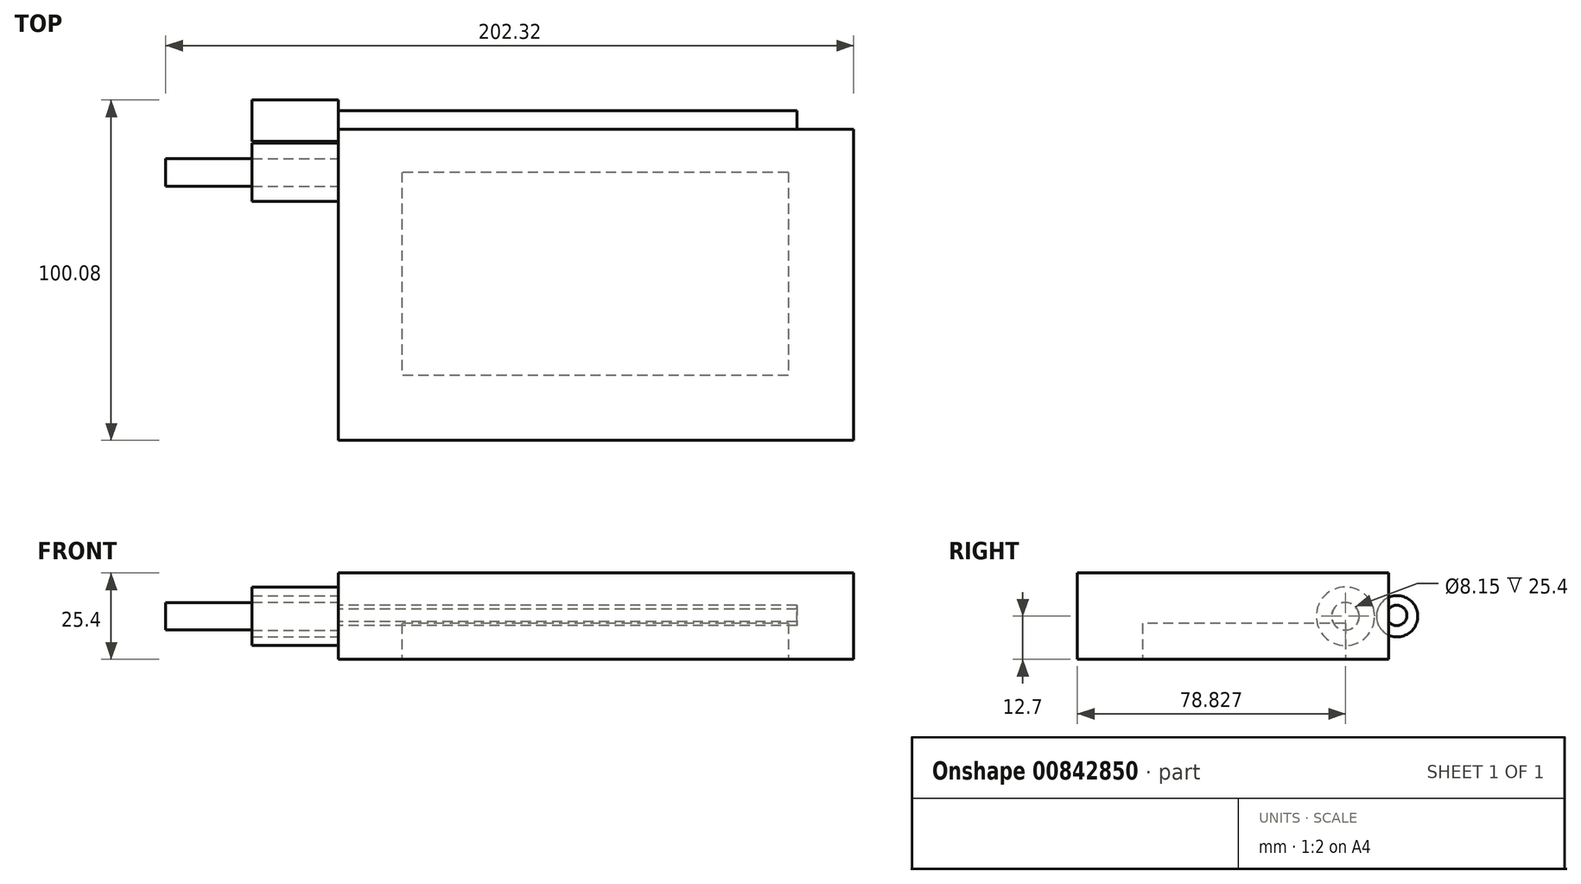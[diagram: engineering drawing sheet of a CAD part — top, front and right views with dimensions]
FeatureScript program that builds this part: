
annotation { "Feature Type Name" : "Feature", "Feature Type Description" : "" }
export const myFeature = defineFeature(function(context is Context, id is Id, definition is map)
    precondition{}
    {
        {
            var Q0;
            Q0=qCreatedBy(makeId("Top.planeOp"),FACE);
            var sketch = newSketch(context, id + "F0", { "sketchPlane" : qUnion([Q0])});
            skLineSegment(sketch, "E0.bottom", {"start": v(-75.46, -48.99) * mm, "end": v(76.06, -48.99) * mm});
            skLineSegment(sketch, "E0.top", {"start": v(-75.46, 42.56) * mm, "end": v(76.06, 42.56) * mm});
            skLineSegment(sketch, "E0.left", {"start": v(-75.46, -48.99) * mm, "end": v(-75.46, 42.56) * mm});
            skLineSegment(sketch, "E0.right", {"start": v(76.06, -48.99) * mm, "end": v(76.06, 42.56) * mm});
            skSolve(sketch);
        }
        {
            var Q0;
            Q0=makeQuery(id+"F0.imprint","IMPRINT",FACE,{"disambiguationData":[TD([[makeQuery(id+"F0.imprint","IMPRINT",EDGE,{"derivedFrom":sQuery(id+"F0.wireOp",EDGE,"E0.bottom")}),1.0]])]});
            extrude(context, id + "F1", {"entities" : qUnion([Q0]), "depth" : 25.4 * mm, "offsetDistance" : 25.4 * mm});
        }
        {
            var Q0;
            Q0=makeQuery(id+"F1.opExtrude","CAP_FACE",FACE,{"disambiguationData":[OSD([sQuery(id+"F0.wireOp",EDGE,"E0.bottom"),sQuery(id+"F0.wireOp",EDGE,"E0.top"),sQuery(id+"F0.wireOp",EDGE,"E0.left"),sQuery(id+"F0.wireOp",EDGE,"E0.right")])],"isStart":true});
            var sketch = newSketch(context, id + "F2", { "sketchPlane" : qUnion([Q0])});
            skLineSegment(sketch, "E1.bottom", {"start": v(56.8, -29.83) * mm, "end": v(-56.8, -29.83) * mm});
            skLineSegment(sketch, "E1.top", {"start": v(56.8, 29.83) * mm, "end": v(-56.8, 29.83) * mm});
            skLineSegment(sketch, "E1.left", {"start": v(56.8, -29.83) * mm, "end": v(56.8, 29.83) * mm});
            skLineSegment(sketch, "E1.right", {"start": v(-56.8, -29.83) * mm, "end": v(-56.8, 29.83) * mm});
            skPoint(sketch, "E1.middle", {"position": v(0, 0) * mm});
            skSolve(sketch);
        }
        {
            var Q0;
            Q0 = qSketchRegion(id + "F2", true);
            extrude(context, id + "F3", {"entities" : qUnion([Q0]), "operationType" : NewBodyOperationType.REMOVE, "oppositeDirection" : true, "depth" : 10.56 * mm, "offsetDistance" : 25.4 * mm});
        }
        {
            var Q0;
            Q0=makeQuery(id+"F1.opExtrude","SWEPT_FACE",FACE,{"disambiguationData":[OSD([sQuery(id+"F0.wireOp",EDGE,"E0.left")])]});
            var sketch = newSketch(context, id + "F4", { "sketchPlane" : qUnion([Q0])});
            skCircle(sketch, "E2", {"center": v(-29.84, 12.7) * mm, "radius": 8.6 * mm});
            skPoint(sketch, "E2.centerSnap0", {"position": v(-42.56, 12.7) * mm});
            skCircle(sketch, "E3", {"center": v(-29.84, 12.7) * mm, "radius": 4.08 * mm});
            skCircle(sketch, "E4", {"center": v(-45.03, 12.7) * mm, "radius": 2.47 * mm});
            skCircle(sketch, "E5", {"center": v(-45.03, 12.7) * mm, "radius": 6.06 * mm});
            skSolve(sketch);
        }
        {
            var Q0;
            {var subQ0=sQuery(id+"F4.wireOp",EDGE,"E5");var subQ1=makeQuery(id+"F1.opExtrude","SWEPT_EDGE",EDGE,{"disambiguationData":[OSD([sQuery(id+"F0.wireOp",EDGE,"E0.top"),sQuery(id+"F0.wireOp",EDGE,"E0.left")])]});var subQ2=makeQuery(id+"F4.imprint","INTERSECT",VERTEX,{"disambiguationData":[OD(0.0)],"derivedFrom":[subQ1,subQ0]});Q0=makeQuery(id+"F4.imprint","IMPRINT",FACE,{"disambiguationData":[TD([[makeQuery(id+"F4.imprint","IMPRINT",EDGE,{"disambiguationData":[TD([[subQ2,-1.0]])],"derivedFrom":subQ0}),1.0]])]});}
            var Q1;
            {var subQ0=sQuery(id+"F4.wireOp",EDGE,"E4");Q1=makeQuery(id+"F4.imprint","IMPRINT",FACE,{"disambiguationData":[TD([[makeQuery(id+"F4.imprint","IMPRINT",EDGE,{"derivedFrom":subQ0}),-1.0]])]});}
            var Q2;
            Q2=makeQuery(id+"F4.imprint","IMPRINT",FACE,{"disambiguationData":[TD([[makeQuery(id+"F4.imprint","IMPRINT",EDGE,{"derivedFrom":sQuery(id+"F4.wireOp",EDGE,"E2")}),1.0]])]});
            extrude(context, id + "F5", {"entities" : qUnion([Q0, Q1, Q2]), "operationType" : NewBodyOperationType.ADD, "depth" : 25.4 * mm, "offsetDistance" : 25.4 * mm});
        }
        {
            var Q0;
            Q0=makeQuery(id+"F5.opExtrude","CAP_FACE",FACE,{"disambiguationData":[OSD([sQuery(id+"F4.wireOp",EDGE,"E2"),sQuery(id+"F4.wireOp",EDGE,"E3")])],"isStart":false});
            var sketch = newSketch(context, id + "F6", { "sketchPlane" : qUnion([Q0])});
            skCircle(sketch, "E6", {"center": v(-29.84, 12.7) * mm, "radius": 4.04 * mm});
            skSolve(sketch);
        }
        {
            var Q0;
            Q0 = qSketchRegion(id + "F6", true);
            extrude(context, id + "F7", {"entities" : qUnion([Q0]), "depth" : 25.4 * mm, "offsetDistance" : 25.4 * mm});
        }
        {
            var Q0;
            Q0=makeQuery(id+"F5.opExtrude","CAP_FACE",FACE,{"disambiguationData":[OSD([sQuery(id+"F4.wireOp",EDGE,"E2"),sQuery(id+"F4.wireOp",EDGE,"E3")])],"isStart":false});
            var sketch = newSketch(context, id + "F8", { "sketchPlane" : qUnion([Q0])});
            skCircle(sketch, "E7", {"center": v(-44.92, 12.95) * mm, "radius": 3.02 * mm});
            skSolve(sketch);
        }
        {
            var Q0;
            Q0 = qSketchRegion(id + "F8", true);
            extrude(context, id + "F9", {"entities" : qUnion([Q0]), "operationType" : NewBodyOperationType.ADD, "oppositeDirection" : true, "depth" : 160.17 * mm, "offsetDistance" : 25.4 * mm});
        }
    });
